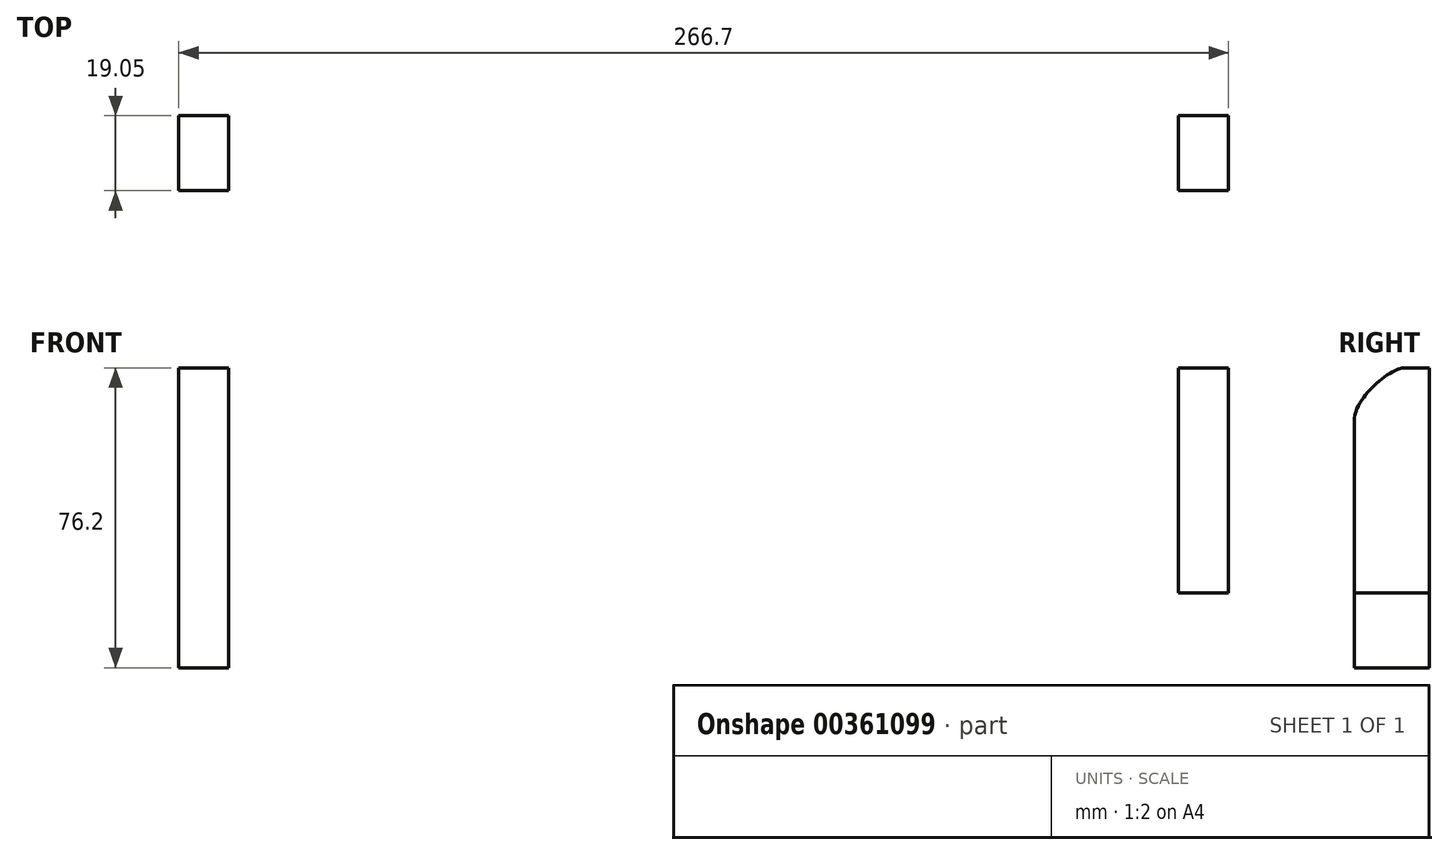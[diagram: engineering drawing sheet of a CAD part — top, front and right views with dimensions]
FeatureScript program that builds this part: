
annotation { "Feature Type Name" : "Feature", "Feature Type Description" : "" }
export const myFeature = defineFeature(function(context is Context, id is Id, definition is map)
    precondition{}
    {
        {
            var Q0;
            Q0=qCreatedBy(makeId("Front.planeOp"),FACE);
            var sketch = newSketch(context, id + "F0", { "sketchPlane" : qUnion([Q0])});
            skLineSegment(sketch, "E0.bottom", {"start": v(0, 0) * mm, "end": v(-266.7, 0) * mm});
            skLineSegment(sketch, "E0.top", {"start": v(0, 285.75) * mm, "end": v(-266.7, 285.75) * mm});
            skLineSegment(sketch, "E0.left", {"start": v(0, 0) * mm, "end": v(0, 285.75) * mm});
            skLineSegment(sketch, "E0.right", {"start": v(-266.7, 0) * mm, "end": v(-266.7, 285.75) * mm});
            skLineSegment(sketch, "E1.bottom", {"start": v(0, 285.75) * mm, "end": v(-12.7, 285.75) * mm});
            skLineSegment(sketch, "E1.top", {"start": v(0, 228.6) * mm, "end": v(-12.7, 228.6) * mm});
            skLineSegment(sketch, "E1.left", {"start": v(0, 285.75) * mm, "end": v(0, 228.6) * mm});
            skLineSegment(sketch, "E1.right", {"start": v(-12.7, 285.75) * mm, "end": v(-12.7, 228.6) * mm});
            skLineSegment(sketch, "E2.bottom", {"start": v(-266.7, 285.75) * mm, "end": v(-254, 285.75) * mm});
            skLineSegment(sketch, "E2.top", {"start": v(-266.7, 209.55) * mm, "end": v(-254, 209.55) * mm});
            skLineSegment(sketch, "E2.left", {"start": v(-266.7, 285.75) * mm, "end": v(-266.7, 209.55) * mm});
            skLineSegment(sketch, "E2.right", {"start": v(-254, 285.75) * mm, "end": v(-254, 209.55) * mm});
            skLineSegment(sketch, "E3.bottom", {"start": v(-266.7, 209.55) * mm, "end": v(0, 209.55) * mm});
            skLineSegment(sketch, "E3.top", {"start": v(-266.7, 0) * mm, "end": v(0, 0) * mm});
            skLineSegment(sketch, "E3.left", {"start": v(-266.7, 209.55) * mm, "end": v(-266.7, 0) * mm});
            skLineSegment(sketch, "E3.right", {"start": v(0, 209.55) * mm, "end": v(0, 0) * mm});
            skLineSegment(sketch, "E4", {"start": v(-133.35, 209.55) * mm, "end": v(-133.35, 285.75) * mm, "construction": true});
            skSolve(sketch);
        }
        {
            var Q0;
            Q0=makeQuery(id+"F0.imprint","IMPRINT",FACE,{"disambiguationData":[TD([[makeQuery(id+"F0.imprint","IMPRINT",EDGE,{"derivedFrom":sQuery(id+"F0.wireOp",EDGE,"E3.top")}),1.0]])]});
            var Q1;
            Q1=makeQuery(id+"F0.imprint","IMPRINT",FACE,{"disambiguationData":[TD([[makeQuery(id+"F0.imprint","IMPRINT",EDGE,{"derivedFrom":sQuery(id+"F0.wireOp",EDGE,"E2.bottom")}),-1.0]])]});
            var Q2;
            Q2=makeQuery(id+"F0.imprint","IMPRINT",FACE,{"disambiguationData":[TD([[makeQuery(id+"F0.imprint","IMPRINT",EDGE,{"derivedFrom":sQuery(id+"F0.wireOp",EDGE,"E1.bottom")}),1.0]])]});
            var Q3;
            Q3=makeQuery(id+"F0.imprint","IMPRINT",FACE,{"disambiguationData":[TD([[makeQuery(id+"F0.imprint","IMPRINT",EDGE,{"derivedFrom":sQuery(id+"F0.wireOp",EDGE,"E0.top")}),1.0]])]});
            extrude(context, id + "F1", {"entities" : qUnion([Q0, Q1, Q2, Q3]), "depth" : 19.05 * mm});
        }
        {
            var Q0;
            Q0=makeQuery(id+"F1.opExtrude","CAP_EDGE",EDGE,{"disambiguationData":[OSD([sQuery(id+"F0.wireOp",EDGE,"E0.top"),sQuery(id+"F0.wireOp",EDGE,"E1.bottom"),sQuery(id+"F0.wireOp",EDGE,"E2.bottom")])],"isStart":false});
            fillet(context, id + "F2", {"entities" : qUnion([Q0]), "radius" : 12.7 * mm, "tangentPropagation" : true, "rho" : 0.25, "crossSection" : FilletCrossSection.CONIC, "allowEdgeOverflow" : false});
        }
    });
